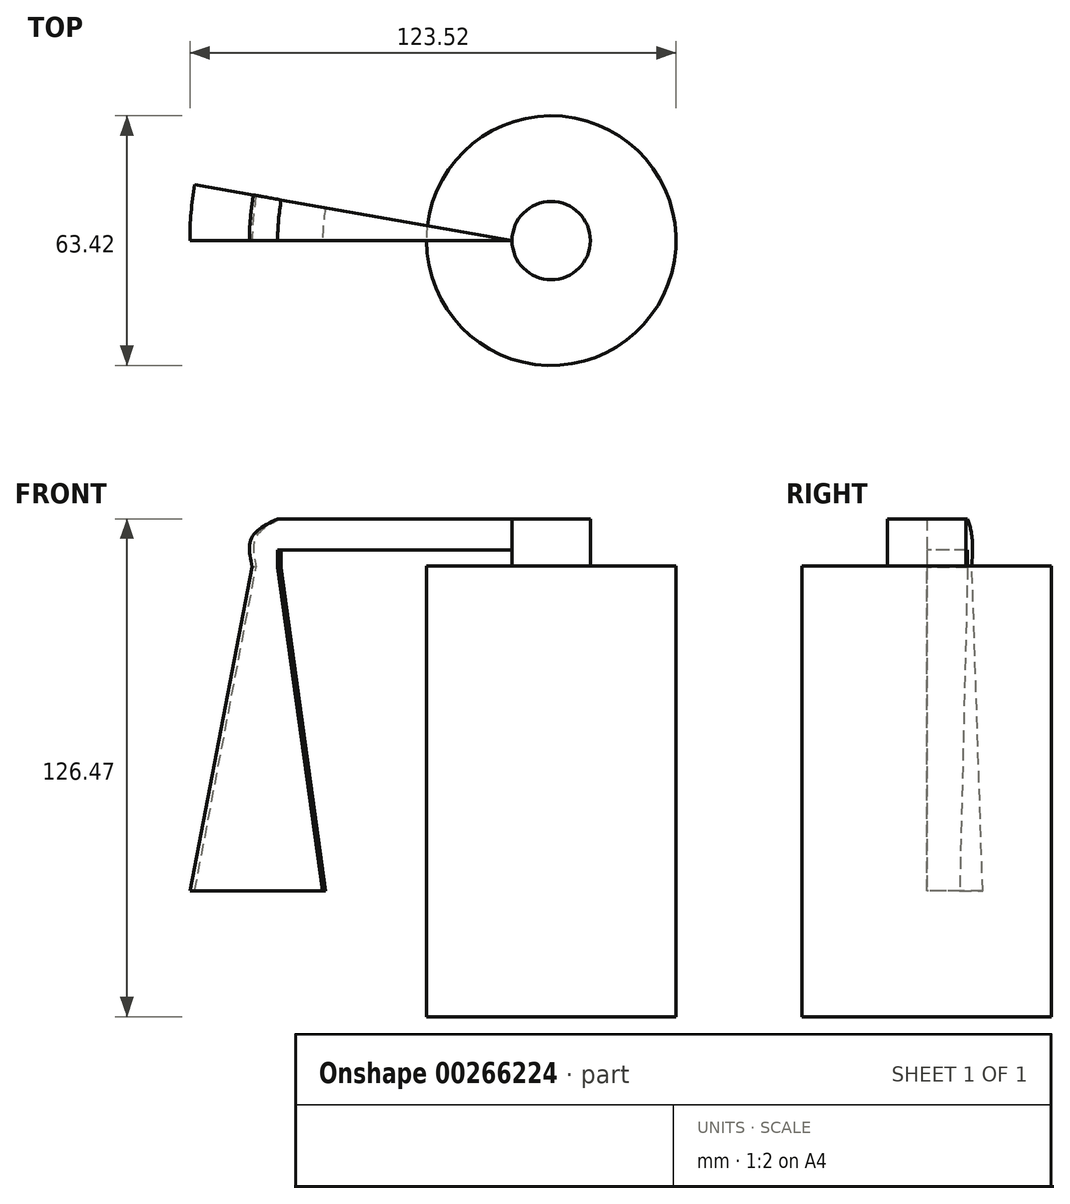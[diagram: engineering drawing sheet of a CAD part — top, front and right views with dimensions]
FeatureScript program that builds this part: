
annotation { "Feature Type Name" : "Feature", "Feature Type Description" : "" }
export const myFeature = defineFeature(function(context is Context, id is Id, definition is map)
    precondition{}
    {
        {
            var Q0;
            Q0=qCreatedBy(makeId("Front.planeOp"),FACE);
            var sketch = newSketch(context, id + "F0", { "sketchPlane" : qUnion([Q0])});
            skLineSegment(sketch, "E0", {"start": v(0, 58.8) * mm, "end": v(-9.96, 58.8) * mm});
            skLineSegment(sketch, "E1", {"start": v(-9.96, 58.8) * mm, "end": v(-9.96, 46.83) * mm});
            skLineSegment(sketch, "E2", {"start": v(-9.96, 46.83) * mm, "end": v(-31.7, 46.83) * mm});
            skLineSegment(sketch, "E3", {"start": v(-31.7, 46.83) * mm, "end": v(-31.7, -67.66) * mm});
            skLineSegment(sketch, "E4", {"start": v(-31.7, -67.66) * mm, "end": v(0, -67.66) * mm});
            skLineSegment(sketch, "E5", {"start": v(0, -67.66) * mm, "end": v(0, 58.8) * mm});
            skLineSegment(sketch, "E6", {"start": v(-9.96, 58.8) * mm, "end": v(-69.5, 58.8) * mm});
            skFitSpline(sketch, "E7", {"points": [v(-69.5, 58.8) * mm, v(-76.14, 54.02) * mm, v(-75.95, 46.64) * mm], "startDerivative": vector(-16.35, -7.86) * mm, "endDerivative": vector(3.62, -16.55) * mm});
            skLineSegment(sketch, "E8", {"start": v(-69.5, 50.88) * mm, "end": v(-9.96, 50.88) * mm});
            skLineSegment(sketch, "E9", {"start": v(-9.96, 50.88) * mm, "end": v(-69.5, 50.88) * mm});
            skLineSegment(sketch, "E10", {"start": v(-69.5, 50.88) * mm, "end": v(-69.5, 46.46) * mm});
            skLineSegment(sketch, "E11", {"start": v(-69.5, 46.46) * mm, "end": v(-58.07, -35.76) * mm});
            skLineSegment(sketch, "E12", {"start": v(-58.07, -35.76) * mm, "end": v(-91.8, -35.76) * mm});
            skLineSegment(sketch, "E13", {"start": v(-91.8, -35.76) * mm, "end": v(-75.95, 46.64) * mm});
            skSolve(sketch);
        }
        {
            var Q0;
            {var subQ3=sQuery(id+"F0.wireOp",EDGE,"E0");Q0=makeQuery(id+"F0.imprint","IMPRINT",FACE,{"disambiguationData":[TD([[makeQuery(id+"F0.imprint","IMPRINT",EDGE,{"derivedFrom":subQ3}),1.0]])]});}
            var Q1;
            Q1=sQuery(id+"F0.wireOp",EDGE,"E5");
            revolve(context, id + "F1", {"entities" : qUnion([Q0]), "axis" : qUnion([Q1]), "revolveType" : RevolveType.FULL});
        }
        {
            var Q0;
            {var subQ1=sQuery(id+"F0.wireOp",EDGE,"E6");Q0=makeQuery(id+"F0.imprint","IMPRINT",FACE,{"disambiguationData":[TD([[makeQuery(id+"F0.imprint","IMPRINT",EDGE,{"derivedFrom":subQ1}),1.0]])]});}
            var Q1;
            Q1=sQuery(id+"F0.wireOp",EDGE,"E1");
            revolve(context, id + "F2", {"entities" : qUnion([Q0]), "axis" : qUnion([Q1]), "revolveType" : RevolveType.ONE_DIRECTION, "angle" : 10 * degree});
        }
    });
